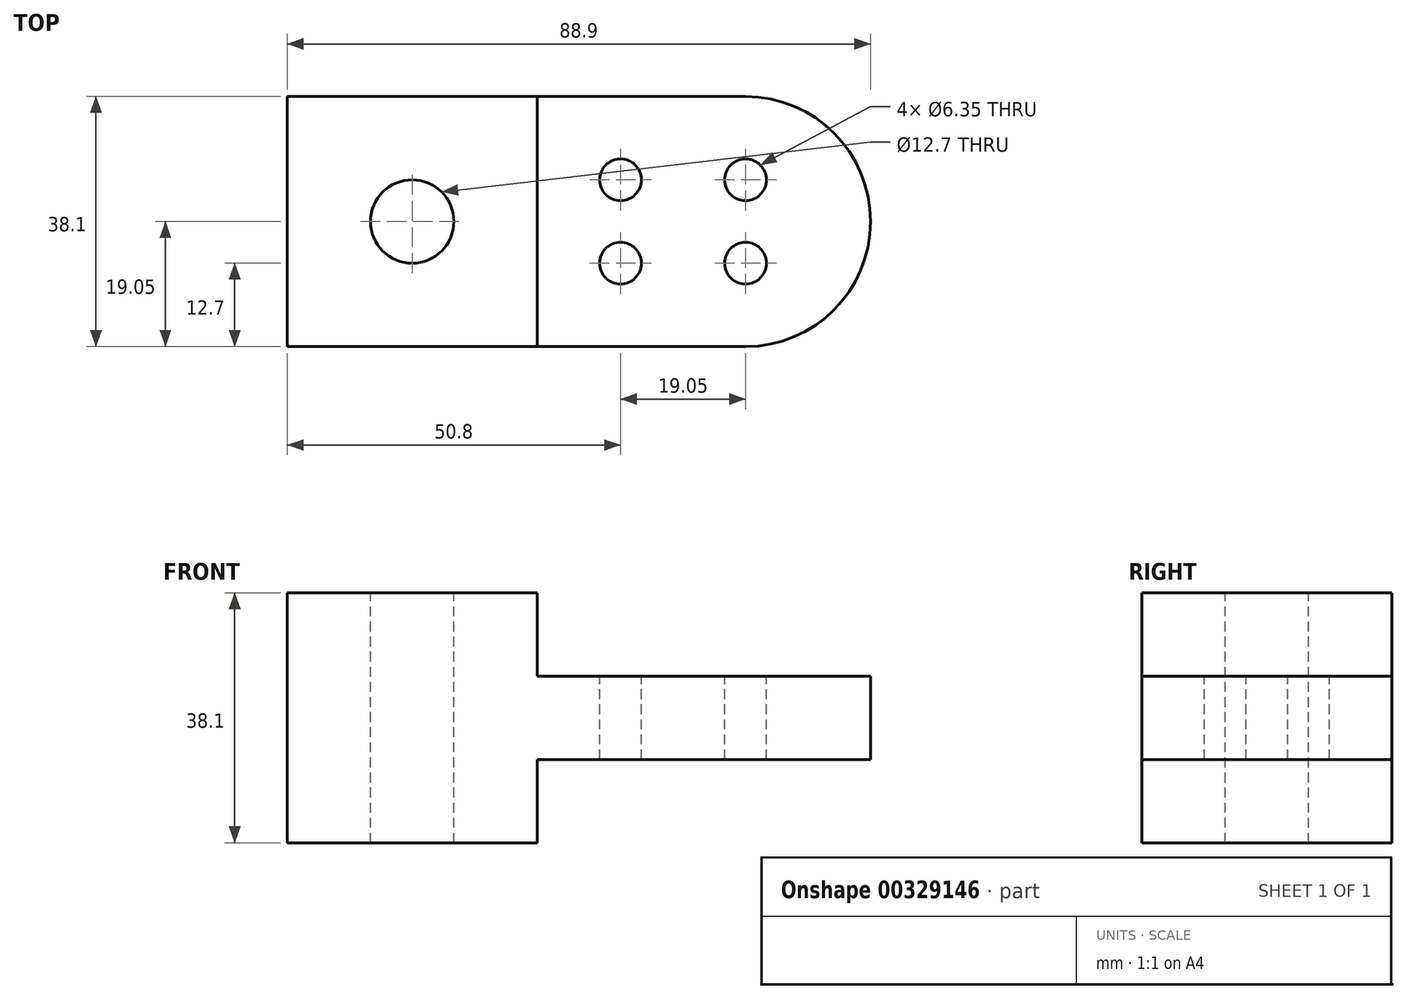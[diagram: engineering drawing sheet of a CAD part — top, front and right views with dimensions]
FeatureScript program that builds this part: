
annotation { "Feature Type Name" : "Feature", "Feature Type Description" : "" }
export const myFeature = defineFeature(function(context is Context, id is Id, definition is map)
    precondition{}
    {
        {
            var Q0;
            Q0=qCreatedBy(makeId("Front.planeOp"),FACE);
            var sketch = newSketch(context, id + "F0", { "sketchPlane" : qUnion([Q0])});
            skLineSegment(sketch, "E0", {"start": v(0, 0) * mm, "end": v(38.1, 0) * mm});
            skLineSegment(sketch, "E1", {"start": v(0, 0) * mm, "end": v(0, 38.1) * mm});
            skLineSegment(sketch, "E2", {"start": v(0, 38.1) * mm, "end": v(38.1, 38.1) * mm});
            skLineSegment(sketch, "E3", {"start": v(38.1, 38.1) * mm, "end": v(38.1, 25.4) * mm});
            skLineSegment(sketch, "E4", {"start": v(38.1, 0) * mm, "end": v(38.1, 12.7) * mm});
            skLineSegment(sketch, "E5", {"start": v(38.1, 12.7) * mm, "end": v(88.9, 12.7) * mm});
            skLineSegment(sketch, "E6", {"start": v(38.1, 25.4) * mm, "end": v(88.9, 25.4) * mm});
            skLineSegment(sketch, "E7", {"start": v(88.9, 25.4) * mm, "end": v(88.9, 12.7) * mm});
            skSolve(sketch);
        }
        {
            var Q0;
            Q0 = qSketchRegion(id + "F0", true);
            extrude(context, id + "F1", {"entities" : qUnion([Q0]), "depth" : 38.1 * mm});
        }
        {
            var Q0;
            Q0=makeQuery(id+"F1.opExtrude","CAP_EDGE",EDGE,{"disambiguationData":[OSD([sQuery(id+"F0.wireOp",EDGE,"E7")])],"isStart":true});
            var Q1;
            Q1=makeQuery(id+"F1.opExtrude","CAP_EDGE",EDGE,{"disambiguationData":[OSD([sQuery(id+"F0.wireOp",EDGE,"E7")])],"isStart":false});
            fillet(context, id + "F2", {"entities" : qUnion([Q0, Q1]), "radius" : 19.05 * mm, "tangentPropagation" : true, "allowEdgeOverflow" : false});
        }
        {
            var Q0;
            Q0=makeQuery(id+"F1.opExtrude","SWEPT_FACE",FACE,{"disambiguationData":[OSD([sQuery(id+"F0.wireOp",EDGE,"E2")])]});
            var sketch = newSketch(context, id + "F3", { "sketchPlane" : qUnion([Q0])});
            skCircle(sketch, "E8", {"center": v(19.05, -19.05) * mm, "radius": 6.35 * mm});
            skSolve(sketch);
        }
        {
            var Q0;
            Q0 = qSketchRegion(id + "F3", true);
            extrude(context, id + "F4", {"entities" : qUnion([Q0]), "operationType" : NewBodyOperationType.REMOVE, "endBound" : BoundingType.THROUGH_ALL, "oppositeDirection" : true, "depth" : 25.4 * mm});
        }
        {
            var Q0;
            Q0=makeQuery(id+"F1.opExtrude","SWEPT_FACE",FACE,{"disambiguationData":[OSD([sQuery(id+"F0.wireOp",EDGE,"E6")])]});
            var sketch = newSketch(context, id + "F5", { "sketchPlane" : qUnion([Q0])});
            skCircle(sketch, "E9", {"center": v(50.8, -12.7) * mm, "radius": 3.18 * mm});
            skCircle(sketch, "E10", {"center": v(69.85, -12.7) * mm, "radius": 3.18 * mm});
            skCircle(sketch, "E11", {"center": v(50.8, -25.4) * mm, "radius": 3.18 * mm});
            skCircle(sketch, "E12", {"center": v(69.85, -25.4) * mm, "radius": 3.18 * mm});
            skSolve(sketch);
        }
        {
            var Q0;
            Q0 = qSketchRegion(id + "F5", true);
            extrude(context, id + "F6", {"entities" : qUnion([Q0]), "operationType" : NewBodyOperationType.REMOVE, "endBound" : BoundingType.THROUGH_ALL, "oppositeDirection" : true, "depth" : 25.4 * mm});
        }
    });
